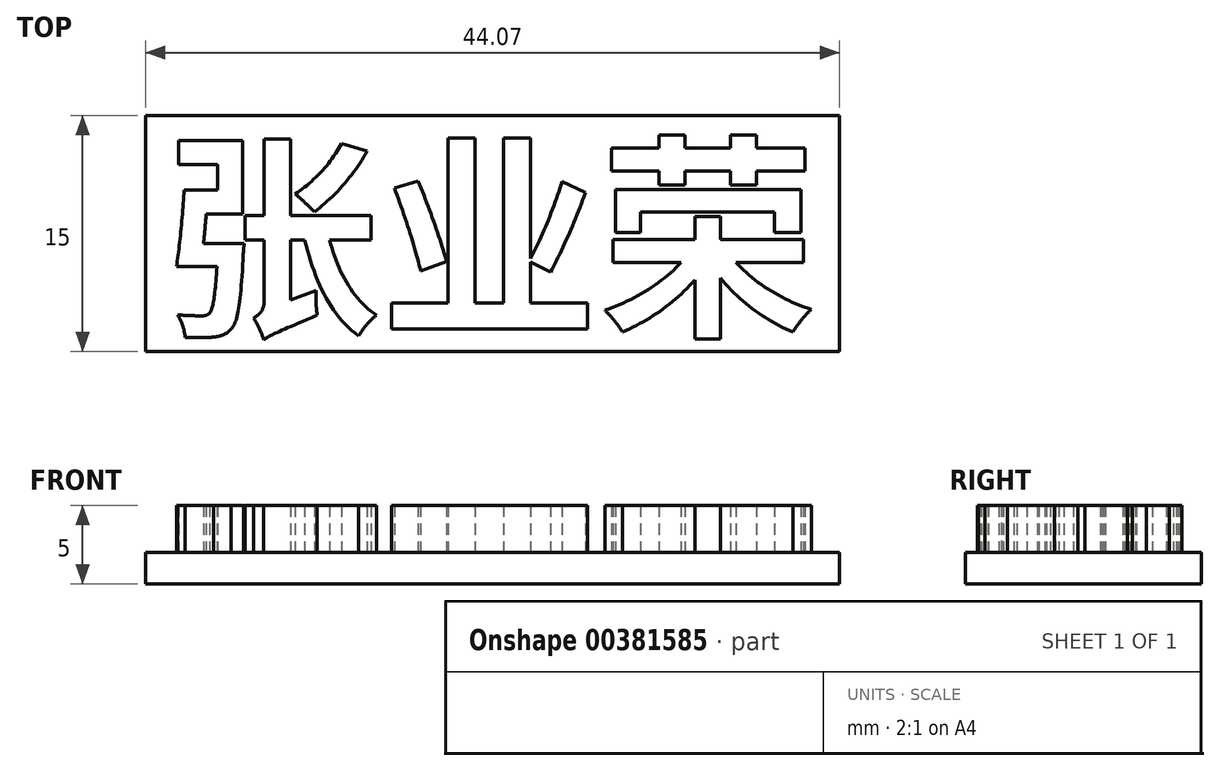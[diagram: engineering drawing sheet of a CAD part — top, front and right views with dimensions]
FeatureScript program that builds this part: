
annotation { "Feature Type Name" : "Feature", "Feature Type Description" : "" }
export const myFeature = defineFeature(function(context is Context, id is Id, definition is map)
    precondition{}
    {
        {
            var Q0;
            Q0=qCreatedBy(makeId("Top.planeOp"),FACE);
            var sketch = newSketch(context, id + "F0", { "sketchPlane" : qUnion([Q0])});
            skText(sketch, "E0", { "text": "张业荣", "fontName": "NotoSansCJKsc-Bold.otf"});
            skLineSegment(sketch, "E1.bottom", {"start": v(-1, 13) * mm, "end": v(43.07, 13) * mm});
            skLineSegment(sketch, "E1.top", {"start": v(-1, -2) * mm, "end": v(43.07, -2) * mm});
            skLineSegment(sketch, "E1.left", {"start": v(-1, 13) * mm, "end": v(-1, -2) * mm});
            skLineSegment(sketch, "E1.right", {"start": v(43.07, 13) * mm, "end": v(43.07, -2) * mm});
            const initialGuessF0  = {"E0": [0, 0, 1, 0, 0.01]};
            skSetInitialGuess(sketch, initialGuessF0);
            skSolve(sketch);
        }
        {
            var Q0;
            Q0=makeQuery(id+"F0.imprint","IMPRINT",FACE,{"disambiguationData":[TD([[makeQuery(id+"F0.imprint","IMPRINT",EDGE,{"derivedFrom":sQuery(id+"F0.wireOp",EDGE,"E0.sketch_text.stroke-0")}),-1.0]])]});
            var Q1;
            Q1=makeQuery(id+"F0.imprint","IMPRINT",FACE,{"disambiguationData":[TD([[makeQuery(id+"F0.imprint","IMPRINT",EDGE,{"derivedFrom":sQuery(id+"F0.wireOp",EDGE,"E0.sketch_text.stroke-0")}),1.0]])]});
            var Q2;
            Q2=makeQuery(id+"F0.imprint","IMPRINT",FACE,{"disambiguationData":[TD([[makeQuery(id+"F0.imprint","IMPRINT",EDGE,{"derivedFrom":sQuery(id+"F0.wireOp",EDGE,"E0.sketch_text.stroke-19")}),1.0]])]});
            var Q3;
            Q3=makeQuery(id+"F0.imprint","IMPRINT",FACE,{"disambiguationData":[TD([[makeQuery(id+"F0.imprint","IMPRINT",EDGE,{"derivedFrom":sQuery(id+"F0.wireOp",EDGE,"E0.sketch_text.stroke-45")}),1.0]])]});
            var Q4;
            Q4=makeQuery(id+"F0.imprint","IMPRINT",FACE,{"disambiguationData":[TD([[makeQuery(id+"F0.imprint","IMPRINT",EDGE,{"derivedFrom":sQuery(id+"F0.wireOp",EDGE,"E0.sketch_text.stroke-41")}),1.0]])]});
            var Q5;
            Q5=makeQuery(id+"F0.imprint","IMPRINT",FACE,{"disambiguationData":[TD([[makeQuery(id+"F0.imprint","IMPRINT",EDGE,{"derivedFrom":sQuery(id+"F0.wireOp",EDGE,"E0.sketch_text.stroke-37")}),1.0]])]});
            var Q6;
            Q6=makeQuery(id+"F0.imprint","IMPRINT",FACE,{"disambiguationData":[TD([[makeQuery(id+"F0.imprint","IMPRINT",EDGE,{"derivedFrom":sQuery(id+"F0.wireOp",EDGE,"E0.sketch_text.stroke-69")}),1.0]])]});
            var Q7;
            Q7=makeQuery(id+"F0.imprint","IMPRINT",FACE,{"disambiguationData":[TD([[makeQuery(id+"F0.imprint","IMPRINT",EDGE,{"derivedFrom":sQuery(id+"F0.wireOp",EDGE,"E0.sketch_text.stroke-69")}),-1.0]])]});
            var Q8;
            Q8=makeQuery(id+"F0.imprint","IMPRINT",FACE,{"disambiguationData":[TD([[makeQuery(id+"F0.imprint","IMPRINT",EDGE,{"derivedFrom":sQuery(id+"F0.wireOp",EDGE,"E0.sketch_text.stroke-49")}),1.0]])]});
            var Q9;
            Q9=makeQuery(id+"F0.imprint","IMPRINT",FACE,{"disambiguationData":[TD([[makeQuery(id+"F0.imprint","IMPRINT",EDGE,{"derivedFrom":sQuery(id+"F0.wireOp",EDGE,"E0.sketch_text.stroke-85")}),1.0]])]});
            var Q10;
            Q10=makeQuery(id+"F0.imprint","IMPRINT",FACE,{"disambiguationData":[TD([[makeQuery(id+"F0.imprint","IMPRINT",EDGE,{"derivedFrom":sQuery(id+"F0.wireOp",EDGE,"E0.sketch_text.stroke-85")}),-1.0]])]});
            var Q11;
            Q11=makeQuery(id+"F0.imprint","IMPRINT",FACE,{"disambiguationData":[TD([[makeQuery(id+"F0.imprint","IMPRINT",EDGE,{"derivedFrom":sQuery(id+"F0.wireOp",EDGE,"E0.sketch_text.stroke-138")}),1.0]])]});
            var Q12;
            Q12=makeQuery(id+"F0.imprint","IMPRINT",FACE,{"disambiguationData":[TD([[makeQuery(id+"F0.imprint","IMPRINT",EDGE,{"derivedFrom":sQuery(id+"F0.wireOp",EDGE,"E0.sketch_text.stroke-142")}),1.0]])]});
            var Q13;
            Q13=makeQuery(id+"F0.imprint","IMPRINT",FACE,{"disambiguationData":[TD([[makeQuery(id+"F0.imprint","IMPRINT",EDGE,{"derivedFrom":sQuery(id+"F0.wireOp",EDGE,"E0.sketch_text.stroke-89")}),1.0]])]});
            var Q14;
            Q14=makeQuery(id+"F0.imprint","IMPRINT",FACE,{"disambiguationData":[TD([[makeQuery(id+"F0.imprint","IMPRINT",EDGE,{"derivedFrom":sQuery(id+"F0.wireOp",EDGE,"E0.sketch_text.stroke-43")}),-1.0]])]});
            var Q15;
            Q15=makeQuery(id+"F0.imprint","IMPRINT",FACE,{"disambiguationData":[TD([[makeQuery(id+"F0.imprint","IMPRINT",EDGE,{"derivedFrom":sQuery(id+"F0.wireOp",EDGE,"E0.sketch_text.stroke-92")}),1.0]])]});
            extrude(context, id + "F1", {"entities" : qUnion([Q0, Q1, Q2, Q3, Q4, Q5, Q6, Q7, Q8, Q9, Q10, Q11, Q12, Q13, Q14, Q15]), "oppositeDirection" : true, "depth" : 2 * mm, "offsetDistance" : 25 * mm});
        }
        {
            var Q0;
            Q0=makeQuery(id+"F0.imprint","IMPRINT",FACE,{"disambiguationData":[TD([[makeQuery(id+"F0.imprint","IMPRINT",EDGE,{"derivedFrom":sQuery(id+"F0.wireOp",EDGE,"E0.sketch_text.stroke-0")}),1.0]])]});
            var Q1;
            Q1=makeQuery(id+"F0.imprint","IMPRINT",FACE,{"disambiguationData":[TD([[makeQuery(id+"F0.imprint","IMPRINT",EDGE,{"derivedFrom":sQuery(id+"F0.wireOp",EDGE,"E0.sketch_text.stroke-19")}),1.0]])]});
            var Q2;
            Q2=makeQuery(id+"F0.imprint","IMPRINT",FACE,{"disambiguationData":[TD([[makeQuery(id+"F0.imprint","IMPRINT",EDGE,{"derivedFrom":sQuery(id+"F0.wireOp",EDGE,"E0.sketch_text.stroke-69")}),1.0]])]});
            var Q3;
            Q3=makeQuery(id+"F0.imprint","IMPRINT",FACE,{"disambiguationData":[TD([[makeQuery(id+"F0.imprint","IMPRINT",EDGE,{"derivedFrom":sQuery(id+"F0.wireOp",EDGE,"E0.sketch_text.stroke-37")}),1.0]])]});
            var Q4;
            Q4=makeQuery(id+"F0.imprint","IMPRINT",FACE,{"disambiguationData":[TD([[makeQuery(id+"F0.imprint","IMPRINT",EDGE,{"derivedFrom":sQuery(id+"F0.wireOp",EDGE,"E0.sketch_text.stroke-41")}),1.0]])]});
            var Q5;
            Q5=makeQuery(id+"F0.imprint","IMPRINT",FACE,{"disambiguationData":[TD([[makeQuery(id+"F0.imprint","IMPRINT",EDGE,{"derivedFrom":sQuery(id+"F0.wireOp",EDGE,"E0.sketch_text.stroke-45")}),1.0]])]});
            var Q6;
            Q6=makeQuery(id+"F0.imprint","IMPRINT",FACE,{"disambiguationData":[TD([[makeQuery(id+"F0.imprint","IMPRINT",EDGE,{"derivedFrom":sQuery(id+"F0.wireOp",EDGE,"E0.sketch_text.stroke-49")}),1.0]])]});
            var Q7;
            Q7=makeQuery(id+"F0.imprint","IMPRINT",FACE,{"disambiguationData":[TD([[makeQuery(id+"F0.imprint","IMPRINT",EDGE,{"derivedFrom":sQuery(id+"F0.wireOp",EDGE,"E0.sketch_text.stroke-138")}),1.0]])]});
            var Q8;
            Q8=makeQuery(id+"F0.imprint","IMPRINT",FACE,{"disambiguationData":[TD([[makeQuery(id+"F0.imprint","IMPRINT",EDGE,{"derivedFrom":sQuery(id+"F0.wireOp",EDGE,"E0.sketch_text.stroke-85")}),1.0]])]});
            var Q9;
            Q9=makeQuery(id+"F0.imprint","IMPRINT",FACE,{"disambiguationData":[TD([[makeQuery(id+"F0.imprint","IMPRINT",EDGE,{"derivedFrom":sQuery(id+"F0.wireOp",EDGE,"E0.sketch_text.stroke-142")}),1.0]])]});
            var Q10;
            Q10=makeQuery(id+"F0.imprint","IMPRINT",FACE,{"disambiguationData":[TD([[makeQuery(id+"F0.imprint","IMPRINT",EDGE,{"derivedFrom":sQuery(id+"F0.wireOp",EDGE,"E0.sketch_text.stroke-89")}),1.0]])]});
            var Q11;
            Q11=makeQuery(id+"F0.imprint","IMPRINT",FACE,{"disambiguationData":[TD([[makeQuery(id+"F0.imprint","IMPRINT",EDGE,{"derivedFrom":sQuery(id+"F0.wireOp",EDGE,"E0.sketch_text.stroke-92")}),1.0]])]});
            extrude(context, id + "F2", {"entities" : qUnion([Q0, Q1, Q2, Q3, Q4, Q5, Q6, Q7, Q8, Q9, Q10, Q11]), "operationType" : NewBodyOperationType.ADD, "depth" : 3 * mm, "offsetDistance" : 25 * mm});
        }
    });
